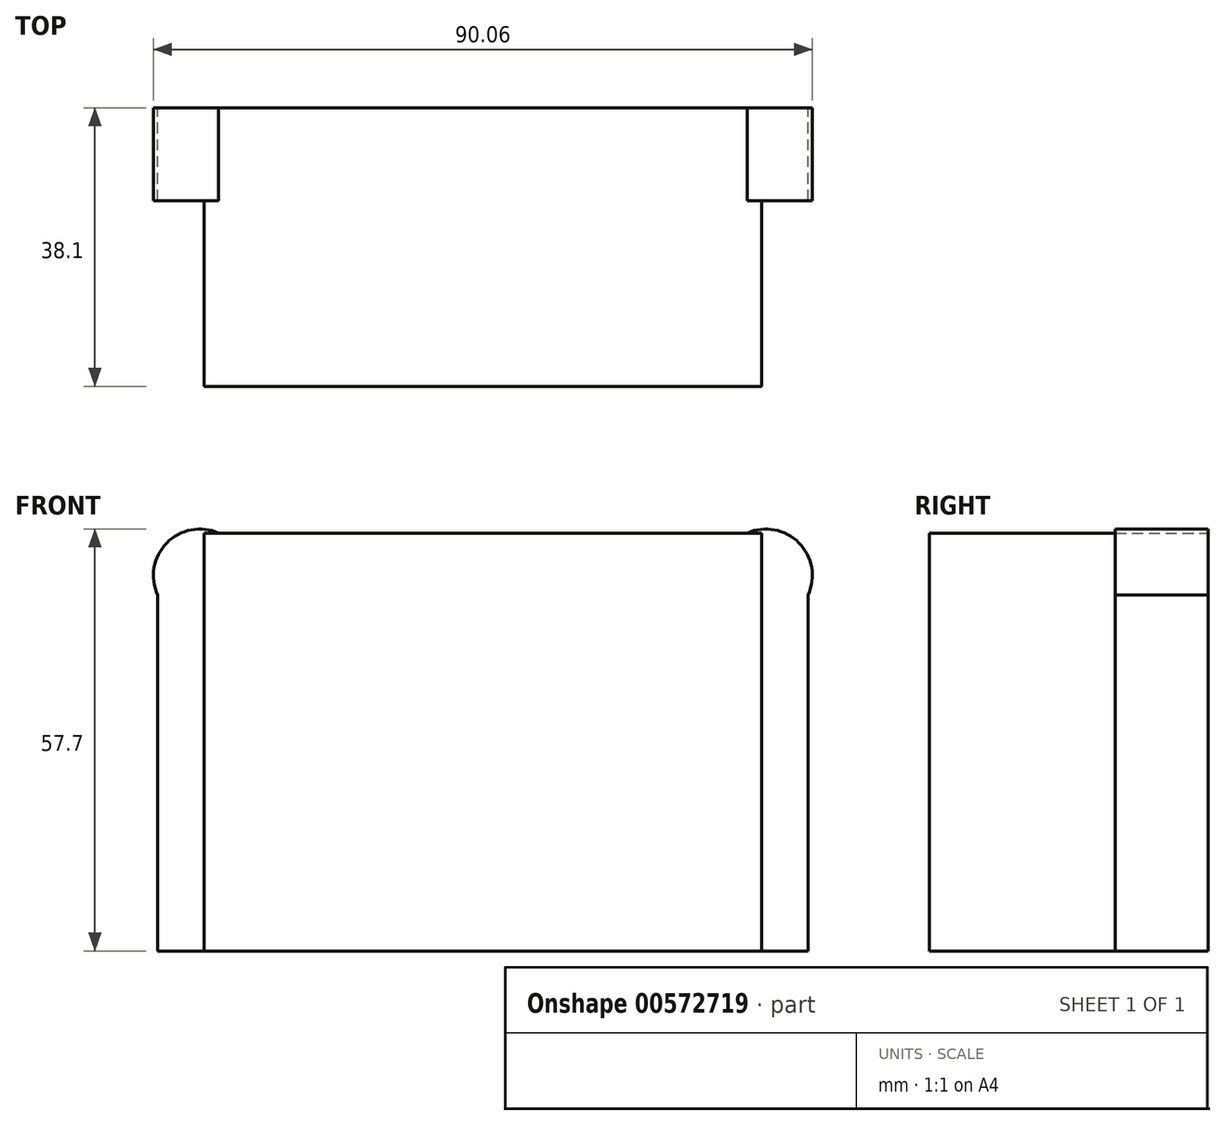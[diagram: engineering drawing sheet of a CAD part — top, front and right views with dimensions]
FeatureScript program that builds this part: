
annotation { "Feature Type Name" : "Feature", "Feature Type Description" : "" }
export const myFeature = defineFeature(function(context is Context, id is Id, definition is map)
    precondition{}
    {
        {
            var Q0;
            Q0=qCreatedBy(makeId("Front.planeOp"),FACE);
            var sketch = newSketch(context, id + "F0", { "sketchPlane" : qUnion([Q0])});
            skLineSegment(sketch, "E0.bottom", {"start": v(-38.1, -25.4) * mm, "end": v(38.1, -25.4) * mm});
            skLineSegment(sketch, "E0.top", {"start": v(-38.1, 25.4) * mm, "end": v(38.1, 25.4) * mm});
            skLineSegment(sketch, "E0.left", {"start": v(-38.1, -25.4) * mm, "end": v(-38.1, 25.4) * mm});
            skLineSegment(sketch, "E0.right", {"start": v(38.1, -25.4) * mm, "end": v(38.1, 25.4) * mm});
            skPoint(sketch, "E0.middle", {"position": v(0, 0) * mm});
            skSolve(sketch);
        }
        {
            var Q0;
            Q0=qCreatedBy(makeId("Front.planeOp"),FACE);
            var sketch = newSketch(context, id + "F1", { "sketchPlane" : qUnion([Q0])});
            skCircle(sketch, "E1", {"center": v(-38.68, 25.95) * mm, "radius": 6.35 * mm});
            skCircle(sketch, "E2.MirrorC", {"center": v(38.68, 25.95) * mm, "radius": 6.35 * mm});
            skSolve(sketch);
        }
        {
            var Q0;
            Q0=qCreatedBy(makeId("Front.planeOp"),FACE);
            var sketch = newSketch(context, id + "F2", { "sketchPlane" : qUnion([Q0])});
            skLineSegment(sketch, "E3.bottom", {"start": v(-38.1, -25.4) * mm, "end": v(-44.45, -25.4) * mm});
            skLineSegment(sketch, "E3.top", {"start": v(-38.1, 25.4) * mm, "end": v(-44.45, 25.4) * mm});
            skLineSegment(sketch, "E3.left", {"start": v(-38.1, -25.4) * mm, "end": v(-38.1, 25.4) * mm});
            skLineSegment(sketch, "E3.right", {"start": v(-44.45, -25.4) * mm, "end": v(-44.45, 25.4) * mm});
            skLineSegment(sketch, "E4.MirrorCS", {"start": v(44.45, -25.4) * mm, "end": v(44.45, 25.4) * mm});
            skLineSegment(sketch, "E5.MirrorCS", {"start": v(38.1, 25.4) * mm, "end": v(44.45, 25.4) * mm});
            skLineSegment(sketch, "E6.MirrorCS", {"start": v(38.1, -25.4) * mm, "end": v(44.45, -25.4) * mm});
            skLineSegment(sketch, "E7.MirrorCS", {"start": v(38.1, -25.4) * mm, "end": v(38.1, 25.4) * mm});
            skLineSegment(sketch, "E8.bottom", {"start": v(-38.1, 25.4) * mm, "end": v(38.1, 25.4) * mm});
            skLineSegment(sketch, "E8.top", {"start": v(-38.1, 31.75) * mm, "end": v(38.1, 31.75) * mm});
            skLineSegment(sketch, "E8.left", {"start": v(-38.1, 25.4) * mm, "end": v(-38.1, 31.75) * mm});
            skLineSegment(sketch, "E8.right", {"start": v(38.1, 25.4) * mm, "end": v(38.1, 31.75) * mm});
            skSolve(sketch);
        }
        {
            var Q0;
            Q0 = qSketchRegion(id + "F0", true);
            var Q1;
            Q1 = qSketchRegion(id + "F1", true);
            var Q2;
            Q2 = qSketchRegion(id + "F2", true);
            extrude(context, id + "F3", {"entities" : qUnion([Q0, Q1, Q2]), "depth" : 12.7 * mm, "offsetDistance" : 25.4 * mm});
        }
        {
            var Q0;
            Q0=makeQuery(id+"F3.opExtrude","CAP_FACE",FACE,{"disambiguationData":[OSD([sQuery(id+"F2.wireOp",EDGE,"E8.bottom"),sQuery(id+"F2.wireOp",EDGE,"E8.top"),sQuery(id+"F2.wireOp",EDGE,"E8.left"),sQuery(id+"F2.wireOp",EDGE,"E8.right")])],"isStart":false});
            var sketch = newSketch(context, id + "F4", { "sketchPlane" : qUnion([Q0])});
            skLineSegment(sketch, "E9.bottom", {"start": v(-38.1, 31.75) * mm, "end": v(38.1, 31.75) * mm});
            skLineSegment(sketch, "E9.top", {"start": v(-38.1, -25.4) * mm, "end": v(38.1, -25.4) * mm});
            skLineSegment(sketch, "E9.left", {"start": v(-38.1, 31.75) * mm, "end": v(-38.1, -25.4) * mm});
            skLineSegment(sketch, "E9.right", {"start": v(38.1, 31.75) * mm, "end": v(38.1, -25.4) * mm});
            skSolve(sketch);
        }
        {
            var Q0;
            Q0 = qSketchRegion(id + "F4", true);
            extrude(context, id + "F5", {"entities" : qUnion([Q0]), "operationType" : NewBodyOperationType.ADD, "depth" : 25.4 * mm, "offsetDistance" : 25.4 * mm});
        }
    });
